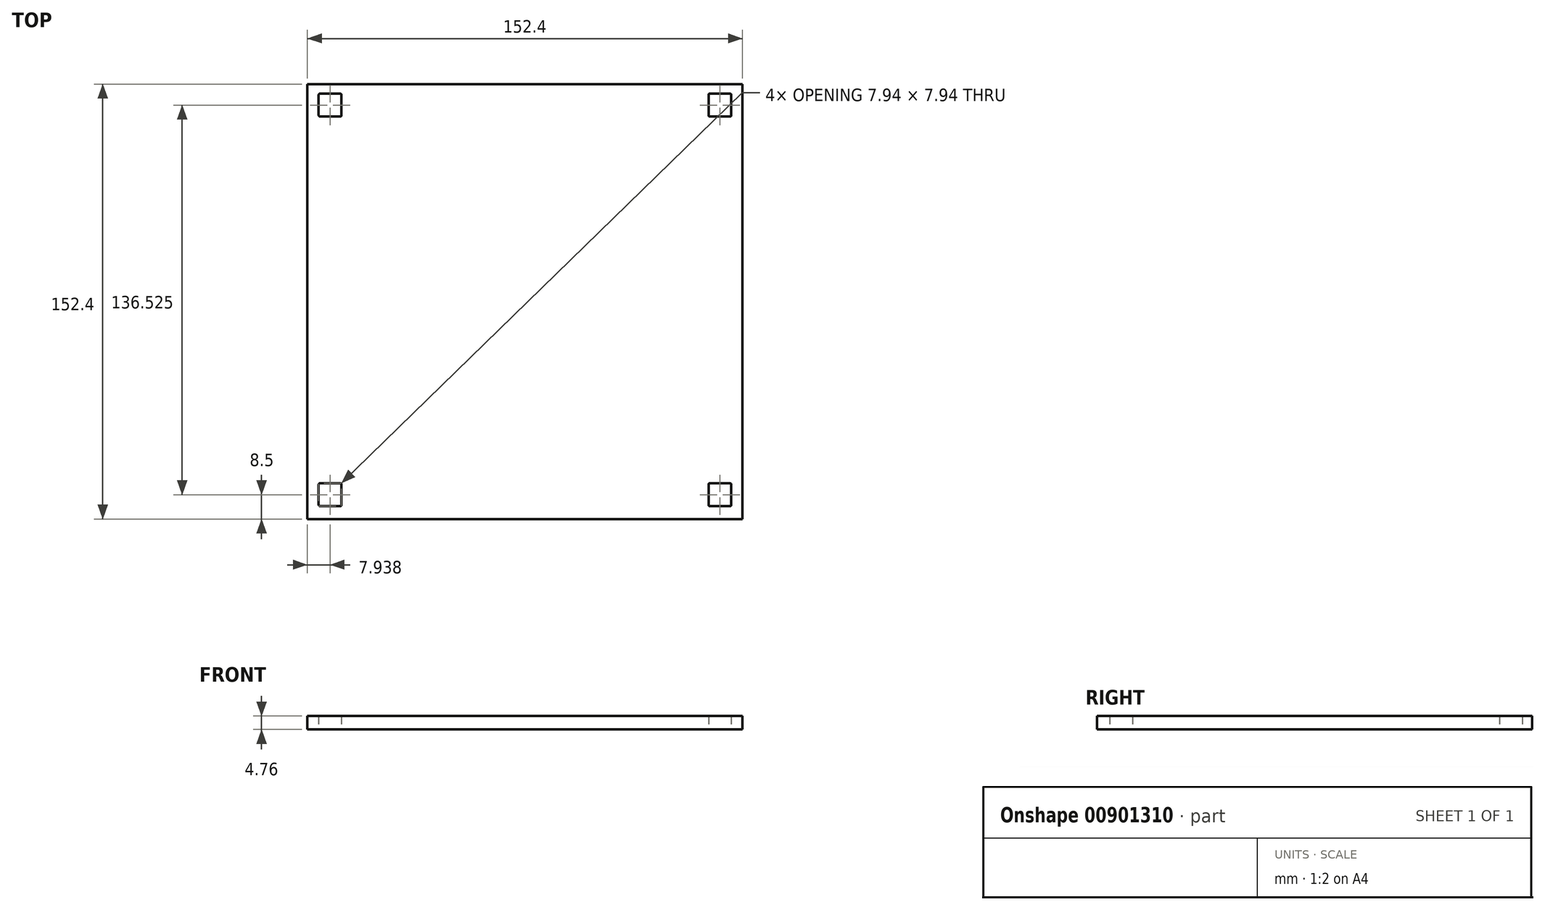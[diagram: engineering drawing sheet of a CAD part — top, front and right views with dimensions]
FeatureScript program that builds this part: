
annotation { "Feature Type Name" : "Feature", "Feature Type Description" : "" }
export const myFeature = defineFeature(function(context is Context, id is Id, definition is map)
    precondition{}
    {
        {
            var Q0;
            Q0=qCreatedBy(makeId("Top.planeOp"),FACE);
            var sketch = newSketch(context, id + "F0", { "sketchPlane" : qUnion([Q0])});
            skLineSegment(sketch, "E0.bottom", {"start": v(0, 0) * mm, "end": v(152.4, 0) * mm});
            skLineSegment(sketch, "E0.top", {"start": v(0, 152.4) * mm, "end": v(152.4, 152.4) * mm});
            skLineSegment(sketch, "E0.left", {"start": v(0, 0) * mm, "end": v(0, 152.4) * mm});
            skLineSegment(sketch, "E0.right", {"start": v(152.4, 0) * mm, "end": v(152.4, 152.4) * mm});
            skLineSegment(sketch, "E1.bottom", {"start": v(19.05, 12.7) * mm, "end": v(133.35, 12.7) * mm, "construction": true});
            skLineSegment(sketch, "E1.top", {"start": v(19.05, 139.7) * mm, "end": v(133.35, 139.7) * mm, "construction": true});
            skLineSegment(sketch, "E1.left", {"start": v(12.7, 19.05) * mm, "end": v(12.7, 133.35) * mm, "construction": true});
            skLineSegment(sketch, "E1.right", {"start": v(139.7, 19.05) * mm, "end": v(139.7, 133.35) * mm, "construction": true});
            skCircle(sketch, "E2", {"center": v(7.94, 8.5) * mm, "radius": 3.97 * mm, "construction": true});
            skPoint(sketch, "E3.visualSharp", {"position": v(12.7, 12.7) * mm});
            skArc(sketch, "E3.filletArc", {"start": v(12.7, 19.05) * mm, "mid": v(14.56, 14.56) * mm, "end": v(19.05, 12.7) * mm, "construction": true});
            skPoint(sketch, "E4.visualSharp", {"position": v(139.7, 12.7) * mm});
            skArc(sketch, "E4.filletArc", {"start": v(133.35, 12.7) * mm, "mid": v(137.84, 14.56) * mm, "end": v(139.7, 19.05) * mm, "construction": true});
            skPoint(sketch, "E5.visualSharp", {"position": v(139.7, 139.7) * mm});
            skArc(sketch, "E5.filletArc", {"start": v(139.7, 133.35) * mm, "mid": v(137.84, 137.84) * mm, "end": v(133.35, 139.7) * mm, "construction": true});
            skCircle(sketch, "E6.0.1.0", {"center": v(7.94, 145.02) * mm, "radius": 3.97 * mm, "construction": true});
            skCircle(sketch, "E6.1.0.0", {"center": v(144.46, 8.5) * mm, "radius": 3.97 * mm, "construction": true});
            skCircle(sketch, "E6.1.1.0", {"center": v(144.46, 145.02) * mm, "radius": 3.97 * mm, "construction": true});
            skLineSegment(sketch, "E6.direction1", {"start": v(7.94, 8.5) * mm, "end": v(144.46, 8.5) * mm, "construction": true});
            skLineSegment(sketch, "E6.direction2", {"start": v(7.94, 8.5) * mm, "end": v(7.94, 145.02) * mm, "construction": true});
            skPoint(sketch, "E7.visualSharp", {"position": v(12.7, 139.7) * mm});
            skArc(sketch, "E7.filletArc", {"start": v(19.05, 139.7) * mm, "mid": v(14.56, 137.84) * mm, "end": v(12.7, 133.35) * mm, "construction": true});
            skLineSegment(sketch, "E8", {"start": v(7.94, 8.5) * mm, "end": v(3.97, 8.5) * mm, "construction": true});
            skLineSegment(sketch, "E9", {"start": v(3.97, 12.15) * mm, "end": v(3.97, 4.85) * mm});
            skLineSegment(sketch, "E10", {"start": v(4.29, 12.47) * mm, "end": v(11.59, 12.47) * mm});
            skLineSegment(sketch, "E11", {"start": v(4.29, 4.53) * mm, "end": v(11.59, 4.53) * mm});
            skLineSegment(sketch, "E12", {"start": v(11.9, 12.15) * mm, "end": v(11.9, 4.85) * mm});
            skPoint(sketch, "E13.visualSharp", {"position": v(3.97, 12.47) * mm});
            skArc(sketch, "E13.filletArc", {"start": v(4.29, 12.47) * mm, "mid": v(4.06, 12.38) * mm, "end": v(3.97, 12.15) * mm});
            skPoint(sketch, "E14.visualSharp", {"position": v(11.9, 12.47) * mm});
            skArc(sketch, "E14.filletArc", {"start": v(11.9, 12.15) * mm, "mid": v(11.81, 12.38) * mm, "end": v(11.59, 12.47) * mm});
            skPoint(sketch, "E15.visualSharp", {"position": v(11.9, 4.53) * mm});
            skArc(sketch, "E15.filletArc", {"start": v(11.59, 4.53) * mm, "mid": v(11.81, 4.62) * mm, "end": v(11.9, 4.85) * mm});
            skPoint(sketch, "E16.visualSharp", {"position": v(3.97, 4.53) * mm});
            skArc(sketch, "E16.filletArc", {"start": v(3.97, 4.85) * mm, "mid": v(4.06, 4.62) * mm, "end": v(4.29, 4.53) * mm});
            skLineSegment(sketch, "E17.0.1.0", {"start": v(4.29, 149) * mm, "end": v(11.59, 149) * mm});
            skArc(sketch, "E17.0.1.1", {"start": v(11.9, 148.68) * mm, "mid": v(11.81, 148.9) * mm, "end": v(11.59, 149) * mm});
            skLineSegment(sketch, "E17.0.1.2", {"start": v(11.9, 148.68) * mm, "end": v(11.9, 141.37) * mm});
            skLineSegment(sketch, "E17.0.1.3", {"start": v(3.97, 148.68) * mm, "end": v(3.97, 141.37) * mm});
            skArc(sketch, "E17.0.1.4", {"start": v(3.97, 141.37) * mm, "mid": v(4.06, 141.15) * mm, "end": v(4.29, 141.06) * mm});
            skLineSegment(sketch, "E17.0.1.5", {"start": v(4.29, 141.06) * mm, "end": v(11.59, 141.06) * mm});
            skArc(sketch, "E17.0.1.6", {"start": v(11.59, 141.06) * mm, "mid": v(11.81, 141.15) * mm, "end": v(11.9, 141.37) * mm});
            skArc(sketch, "E17.0.1.7", {"start": v(4.29, 149) * mm, "mid": v(4.06, 148.9) * mm, "end": v(3.97, 148.68) * mm});
            skLineSegment(sketch, "E17.1.0.0", {"start": v(140.81, 12.47) * mm, "end": v(148.11, 12.47) * mm});
            skArc(sketch, "E17.1.0.1", {"start": v(148.43, 12.15) * mm, "mid": v(148.34, 12.38) * mm, "end": v(148.11, 12.47) * mm});
            skLineSegment(sketch, "E17.1.0.2", {"start": v(148.43, 12.15) * mm, "end": v(148.43, 4.85) * mm});
            skLineSegment(sketch, "E17.1.0.3", {"start": v(140.5, 12.15) * mm, "end": v(140.5, 4.85) * mm});
            skArc(sketch, "E17.1.0.4", {"start": v(140.5, 4.85) * mm, "mid": v(140.59, 4.62) * mm, "end": v(140.81, 4.53) * mm});
            skLineSegment(sketch, "E17.1.0.5", {"start": v(140.81, 4.53) * mm, "end": v(148.11, 4.53) * mm});
            skArc(sketch, "E17.1.0.6", {"start": v(148.11, 4.53) * mm, "mid": v(148.34, 4.62) * mm, "end": v(148.43, 4.85) * mm});
            skArc(sketch, "E17.1.0.7", {"start": v(140.81, 12.47) * mm, "mid": v(140.59, 12.38) * mm, "end": v(140.5, 12.15) * mm});
            skLineSegment(sketch, "E17.1.1.0", {"start": v(140.81, 149) * mm, "end": v(148.11, 149) * mm});
            skArc(sketch, "E17.1.1.1", {"start": v(148.43, 148.68) * mm, "mid": v(148.34, 148.9) * mm, "end": v(148.11, 149) * mm});
            skLineSegment(sketch, "E17.1.1.2", {"start": v(148.43, 148.68) * mm, "end": v(148.43, 141.37) * mm});
            skLineSegment(sketch, "E17.1.1.3", {"start": v(140.5, 148.68) * mm, "end": v(140.5, 141.37) * mm});
            skArc(sketch, "E17.1.1.4", {"start": v(140.5, 141.37) * mm, "mid": v(140.59, 141.15) * mm, "end": v(140.81, 141.06) * mm});
            skLineSegment(sketch, "E17.1.1.5", {"start": v(140.81, 141.06) * mm, "end": v(148.11, 141.06) * mm});
            skArc(sketch, "E17.1.1.6", {"start": v(148.11, 141.06) * mm, "mid": v(148.34, 141.15) * mm, "end": v(148.43, 141.37) * mm});
            skArc(sketch, "E17.1.1.7", {"start": v(140.81, 149) * mm, "mid": v(140.59, 148.9) * mm, "end": v(140.5, 148.68) * mm});
            skLineSegment(sketch, "E17.direction1", {"start": v(4.29, 12.47) * mm, "end": v(140.81, 12.47) * mm, "construction": true});
            skLineSegment(sketch, "E17.direction2", {"start": v(4.29, 12.47) * mm, "end": v(4.29, 149) * mm, "construction": true});
            skSolve(sketch);
        }
        {
            var Q0;
            Q0=makeQuery(id+"F0.imprint","IMPRINT",FACE,{"disambiguationData":[TD([[makeQuery(id+"F0.imprint","IMPRINT",EDGE,{"derivedFrom":sQuery(id+"F0.wireOp",EDGE,"E0.bottom")}),1.0]])]});
            extrude(context, id + "F1", {"entities" : qUnion([Q0]), "depth" : 4.76 * mm, "offsetDistance" : 25.4 * mm});
        }
    });
